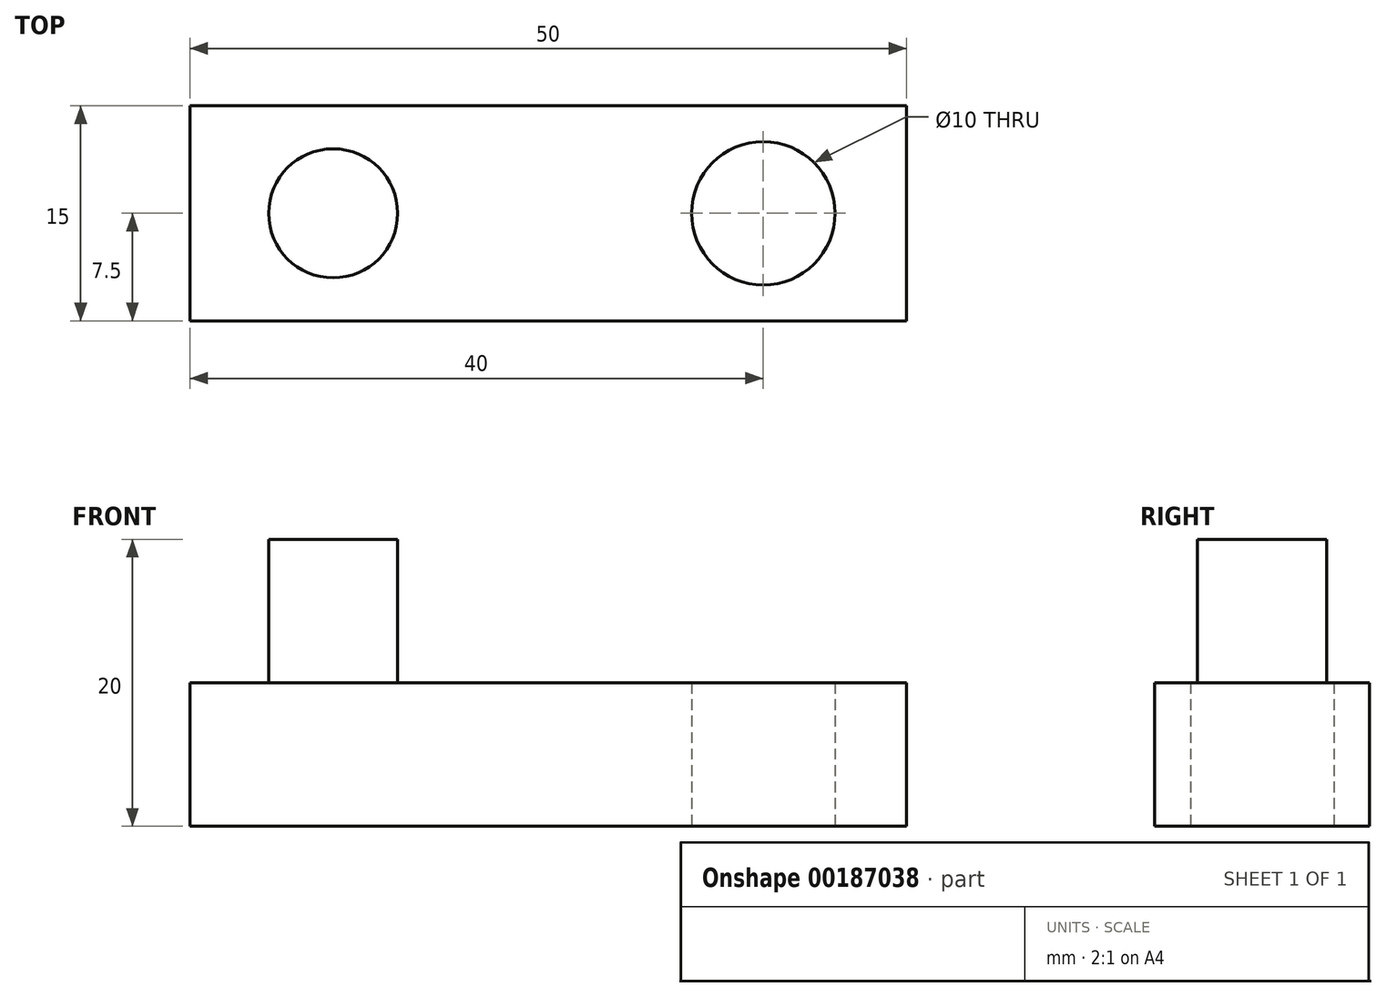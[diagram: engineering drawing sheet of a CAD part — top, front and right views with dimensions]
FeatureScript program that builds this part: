
annotation { "Feature Type Name" : "Feature", "Feature Type Description" : "" }
export const myFeature = defineFeature(function(context is Context, id is Id, definition is map)
    precondition{}
    {
        {
            var Q0;
            Q0=qCreatedBy(makeId("Top.planeOp"),FACE);
            var sketch = newSketch(context, id + "F0", { "sketchPlane" : qUnion([Q0])});
            skLineSegment(sketch, "E0.bottom", {"start": v(-25, 7.5) * mm, "end": v(25, 7.5) * mm});
            skLineSegment(sketch, "E0.top", {"start": v(-25, -7.5) * mm, "end": v(25, -7.5) * mm});
            skLineSegment(sketch, "E0.left", {"start": v(-25, 7.5) * mm, "end": v(-25, -7.5) * mm});
            skLineSegment(sketch, "E0.right", {"start": v(25, 7.5) * mm, "end": v(25, -7.5) * mm});
            skPoint(sketch, "E0.middle", {"position": v(0, 0) * mm});
            skCircle(sketch, "E1", {"center": v(15, 0) * mm, "radius": 5 * mm});
            skSolve(sketch);
        }
        {
            var Q0;
            Q0=makeQuery(id+"F0.imprint","IMPRINT",FACE,{"disambiguationData":[TD([[makeQuery(id+"F0.imprint","IMPRINT",EDGE,{"derivedFrom":sQuery(id+"F0.wireOp",EDGE,"E0.bottom")}),-1.0]])]});
            extrude(context, id + "F1", {"entities" : qUnion([Q0]), "depth" : 10 * mm});
        }
        {
            var Q0;
            Q0=makeQuery(id+"F1.opExtrude","CAP_FACE",FACE,{"disambiguationData":[OSD([sQuery(id+"F0.wireOp",EDGE,"E0.bottom"),sQuery(id+"F0.wireOp",EDGE,"E0.top"),sQuery(id+"F0.wireOp",EDGE,"E0.left"),sQuery(id+"F0.wireOp",EDGE,"E0.right"),sQuery(id+"F0.wireOp",EDGE,"E1")])],"isStart":false});
            var sketch = newSketch(context, id + "F2", { "sketchPlane" : qUnion([Q0])});
            skCircle(sketch, "E2", {"center": v(-15, 0) * mm, "radius": 4.5 * mm});
            skSolve(sketch);
        }
        {
            var Q0;
            Q0=makeQuery(id+"F2.imprint","IMPRINT",FACE,{"disambiguationData":[TD([[makeQuery(id+"F2.imprint","IMPRINT",EDGE,{"derivedFrom":sQuery(id+"F2.wireOp",EDGE,"E2")}),1.0]])]});
            extrude(context, id + "F3", {"entities" : qUnion([Q0]), "operationType" : NewBodyOperationType.ADD, "depth" : 10 * mm});
        }
    });
